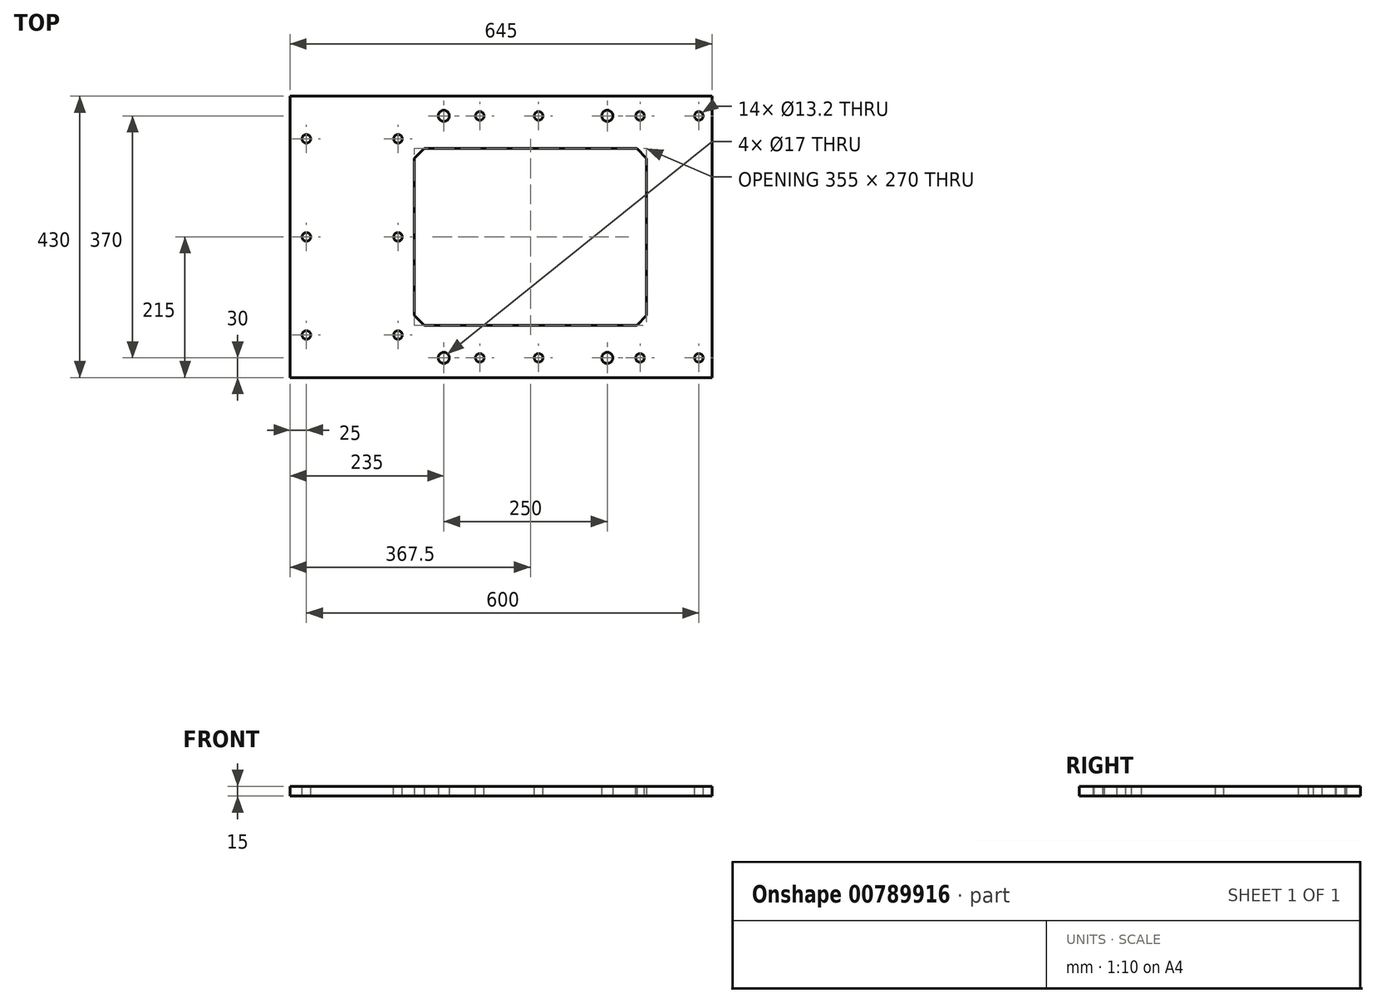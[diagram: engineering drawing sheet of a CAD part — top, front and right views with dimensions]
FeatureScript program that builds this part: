
annotation { "Feature Type Name" : "Feature", "Feature Type Description" : "" }
export const myFeature = defineFeature(function(context is Context, id is Id, definition is map)
    precondition{}
    {
        {
            var Q0;
            Q0=qCreatedBy(makeId("Top.planeOp"),FACE);
            var sketch = newSketch(context, id + "F0", { "sketchPlane" : qUnion([Q0])});
            skLineSegment(sketch, "E0.bottom", {"start": v(322.5, 215) * mm, "end": v(-322.5, 215) * mm});
            skLineSegment(sketch, "E0.top", {"start": v(322.5, -215) * mm, "end": v(-322.5, -215) * mm});
            skLineSegment(sketch, "E0.left", {"start": v(322.5, 215) * mm, "end": v(322.5, -215) * mm});
            skLineSegment(sketch, "E0.right", {"start": v(-322.5, 215) * mm, "end": v(-322.5, -215) * mm});
            skPoint(sketch, "E0.middle", {"position": v(0, 0) * mm});
            skLineSegment(sketch, "E1.bottom", {"start": v(-117.5, 135) * mm, "end": v(207.5, 135) * mm});
            skLineSegment(sketch, "E1.top", {"start": v(-117.5, -135) * mm, "end": v(207.5, -135) * mm});
            skLineSegment(sketch, "E1.left", {"start": v(-132.5, 120) * mm, "end": v(-132.5, -120) * mm});
            skLineSegment(sketch, "E1.right", {"start": v(222.5, 120) * mm, "end": v(222.5, -120) * mm});
            skLineSegment(sketch, "E2", {"start": v(-132.5, 120) * mm, "end": v(-117.5, 135) * mm});
            skLineSegment(sketch, "E3", {"start": v(207.5, 135) * mm, "end": v(222.5, 120) * mm});
            skLineSegment(sketch, "E4", {"start": v(-132.5, -120) * mm, "end": v(-117.5, -135) * mm});
            skLineSegment(sketch, "E5", {"start": v(207.5, -135) * mm, "end": v(222.5, -120) * mm});
            skSolve(sketch);
        }
        {
            var Q0;
            Q0=qSketchRegion(id+"F0",true);
            extrude(context, id + "F1", {"entities" : qUnion([Q0]), "depth" : 15 * mm, "offsetDistance" : 25 * mm});
        }
        {
            var Q0;
            Q0=qCreatedBy(makeId("Top.planeOp"),FACE);
            var sketch = newSketch(context, id + "F2", { "sketchPlane" : qUnion([Q0])});
            skLineSegment(sketch, "E6.0", {"start": v(322.5, 215) * mm, "end": v(-322.5, 215) * mm, "construction": true});
            skLineSegment(sketch, "E7.0", {"start": v(322.5, 215) * mm, "end": v(322.5, -215) * mm, "construction": true});
            skLineSegment(sketch, "E8.0", {"start": v(322.5, -215) * mm, "end": v(-322.5, -215) * mm, "construction": true});
            skLineSegment(sketch, "E9.0", {"start": v(-322.5, 215) * mm, "end": v(-322.5, -215) * mm, "construction": true});
            skLineSegment(sketch, "E10", {"start": v(-297.5, 215) * mm, "end": v(-297.5, -215) * mm, "construction": true});
            skLineSegment(sketch, "E11", {"start": v(-157.5, 215) * mm, "end": v(-157.5, -215) * mm, "construction": true});
            skLineSegment(sketch, "E12", {"start": v(-32.5, 215) * mm, "end": v(-32.5, -215) * mm, "construction": true});
            skLineSegment(sketch, "E13", {"start": v(57.5, 215) * mm, "end": v(57.5, -215) * mm, "construction": true});
            skLineSegment(sketch, "E14", {"start": v(212.5, 215) * mm, "end": v(212.5, -215) * mm, "construction": true});
            skLineSegment(sketch, "E15", {"start": v(302.5, 215) * mm, "end": v(302.5, -215) * mm, "construction": true});
            skLineSegment(sketch, "E16", {"start": v(322.5, 185) * mm, "end": v(-322.5, 185) * mm, "construction": true});
            skLineSegment(sketch, "E17", {"start": v(322.5, -185) * mm, "end": v(-322.5, -185) * mm, "construction": true});
            skPoint(sketch, "E18", {"position": v(302.5, 185) * mm});
            skPoint(sketch, "E19", {"position": v(212.5, 185) * mm});
            skPoint(sketch, "E20", {"position": v(57.5, 185) * mm});
            skPoint(sketch, "E21", {"position": v(-32.5, 185) * mm});
            skPoint(sketch, "E22", {"position": v(-32.5, -185) * mm});
            skPoint(sketch, "E23", {"position": v(57.5, -185) * mm});
            skPoint(sketch, "E24", {"position": v(302.5, -185) * mm});
            skPoint(sketch, "E25", {"position": v(212.5, -185) * mm});
            skLineSegment(sketch, "E26", {"start": v(-322.5, 150) * mm, "end": v(-157.5, 150) * mm, "construction": true});
            skLineSegment(sketch, "E27", {"start": v(-322.5, 0) * mm, "end": v(-157.5, 0) * mm, "construction": true});
            skLineSegment(sketch, "E28", {"start": v(-322.5, -150) * mm, "end": v(-157.5, -150) * mm, "construction": true});
            skPoint(sketch, "E29", {"position": v(-157.5, 150) * mm});
            skPoint(sketch, "E30", {"position": v(-297.5, 150) * mm});
            skPoint(sketch, "E31", {"position": v(-157.5, 0) * mm});
            skPoint(sketch, "E32", {"position": v(-297.5, 0) * mm});
            skPoint(sketch, "E33", {"position": v(-297.5, -150) * mm});
            skPoint(sketch, "E34", {"position": v(-157.5, -150) * mm});
            skSolve(sketch);
        }
        {
            var Q0;
            Q0=sQuery(id+"F2.wireOp",VERTEX,"E30");
            var Q1;
            Q1=sQuery(id+"F2.wireOp",VERTEX,"E32");
            var Q2;
            Q2=sQuery(id+"F2.wireOp",VERTEX,"E33");
            var Q3;
            Q3=sQuery(id+"F2.wireOp",VERTEX,"E29");
            var Q4;
            Q4=sQuery(id+"F2.wireOp",VERTEX,"E31");
            var Q5;
            Q5=sQuery(id+"F2.wireOp",VERTEX,"E34");
            var Q6;
            Q6=sQuery(id+"F2.wireOp",VERTEX,"E22");
            var Q7;
            Q7=sQuery(id+"F2.wireOp",VERTEX,"E23");
            var Q8;
            Q8=sQuery(id+"F2.wireOp",VERTEX,"E25");
            var Q9;
            Q9=sQuery(id+"F2.wireOp",VERTEX,"E24");
            var Q10;
            Q10=sQuery(id+"F2.wireOp",VERTEX,"E18");
            var Q11;
            Q11=sQuery(id+"F2.wireOp",VERTEX,"E19");
            var Q12;
            Q12=sQuery(id+"F2.wireOp",VERTEX,"E20");
            var Q13;
            Q13=sQuery(id+"F2.wireOp",VERTEX,"E21");
            var Q14;
            Q14=makeQuery(id+"F1.opExtrude","SWEPT_BODY",BODY,{"disambiguationData":[OSD([sQuery(id+"F0.wireOp",EDGE,"E0.bottom"),sQuery(id+"F0.wireOp",EDGE,"E0.top"),sQuery(id+"F0.wireOp",EDGE,"E0.left"),sQuery(id+"F0.wireOp",EDGE,"E0.right"),sQuery(id+"F0.wireOp",EDGE,"E1.bottom"),sQuery(id+"F0.wireOp",EDGE,"E1.top"),sQuery(id+"F0.wireOp",EDGE,"E1.left"),sQuery(id+"F0.wireOp",EDGE,"E1.right"),sQuery(id+"F0.wireOp",EDGE,"E2"),sQuery(id+"F0.wireOp",EDGE,"E3"),sQuery(id+"F0.wireOp",EDGE,"E4"),sQuery(id+"F0.wireOp",EDGE,"E5")])]});
            hole(context, id + "F3", {"style" : HoleStyle.SIMPLE, "endStyle" : HoleEndStyle.THROUGH, "oppositeDirection" : true, "standardTappedOrClearance" : lookupTablePath({ "standard" : "ISO", "fit" : "Normal", "size" : "M12", "type" : "Clearance" }), "standardBlindInLast" : lookupTablePath({ "fit" : "Standard", "standard" : "ISO", "size" : "M12", "type" : "Clearance" }), "holeDiameter" : 13.2 * mm, "majorDiameter" : 5 * mm, "isTappedThrough" : true, "tappedDepth" : 12 * mm, "tapClearance" : 3, "locations" : qUnion([Q0, Q1, Q2, Q3, Q4, Q5, Q6, Q7, Q8, Q9, Q10, Q11, Q12, Q13]), "scope" : qUnion([Q14]), "startStyle" : HoleStartStyle.PART});
        }
        {
            var Q0;
            Q0=qCreatedBy(makeId("Top.planeOp"),FACE);
            var sketch = newSketch(context, id + "F4", { "sketchPlane" : qUnion([Q0])});
            skLineSegment(sketch, "E35.0", {"start": v(322.5, 215) * mm, "end": v(-322.5, 215) * mm, "construction": true});
            skLineSegment(sketch, "E36.0", {"start": v(322.5, 215) * mm, "end": v(322.5, -215) * mm, "construction": true});
            skLineSegment(sketch, "E37.0", {"start": v(322.5, -215) * mm, "end": v(-322.5, -215) * mm, "construction": true});
            skLineSegment(sketch, "E38.0", {"start": v(-322.5, 215) * mm, "end": v(-322.5, -215) * mm, "construction": true});
            skLineSegment(sketch, "E39", {"start": v(322.5, -185) * mm, "end": v(-322.5, -185) * mm, "construction": true});
            skLineSegment(sketch, "E40", {"start": v(322.5, 185) * mm, "end": v(-322.5, 185) * mm, "construction": true});
            skLineSegment(sketch, "E41", {"start": v(162.5, 215) * mm, "end": v(162.5, -215) * mm, "construction": true});
            skLineSegment(sketch, "E42", {"start": v(-87.5, 215) * mm, "end": v(-87.5, -215) * mm, "construction": true});
            skCircle(sketch, "E43", {"center": v(-87.5, 185) * mm, "radius": 8.5 * mm});
            skCircle(sketch, "E44", {"center": v(162.5, 185) * mm, "radius": 8.5 * mm});
            skCircle(sketch, "E45", {"center": v(162.5, -185) * mm, "radius": 8.5 * mm});
            skCircle(sketch, "E46", {"center": v(-87.5, -185) * mm, "radius": 8.5 * mm});
            skSolve(sketch);
        }
        {
            var Q0;
            Q0=qSketchRegion(id+"F4",true);
            extrude(context, id + "F5", {"entities" : qUnion([Q0]), "operationType" : NewBodyOperationType.REMOVE, "endBound" : BoundingType.UP_TO_NEXT, "depth" : 25 * mm, "offsetDistance" : 25 * mm});
        }
    });
